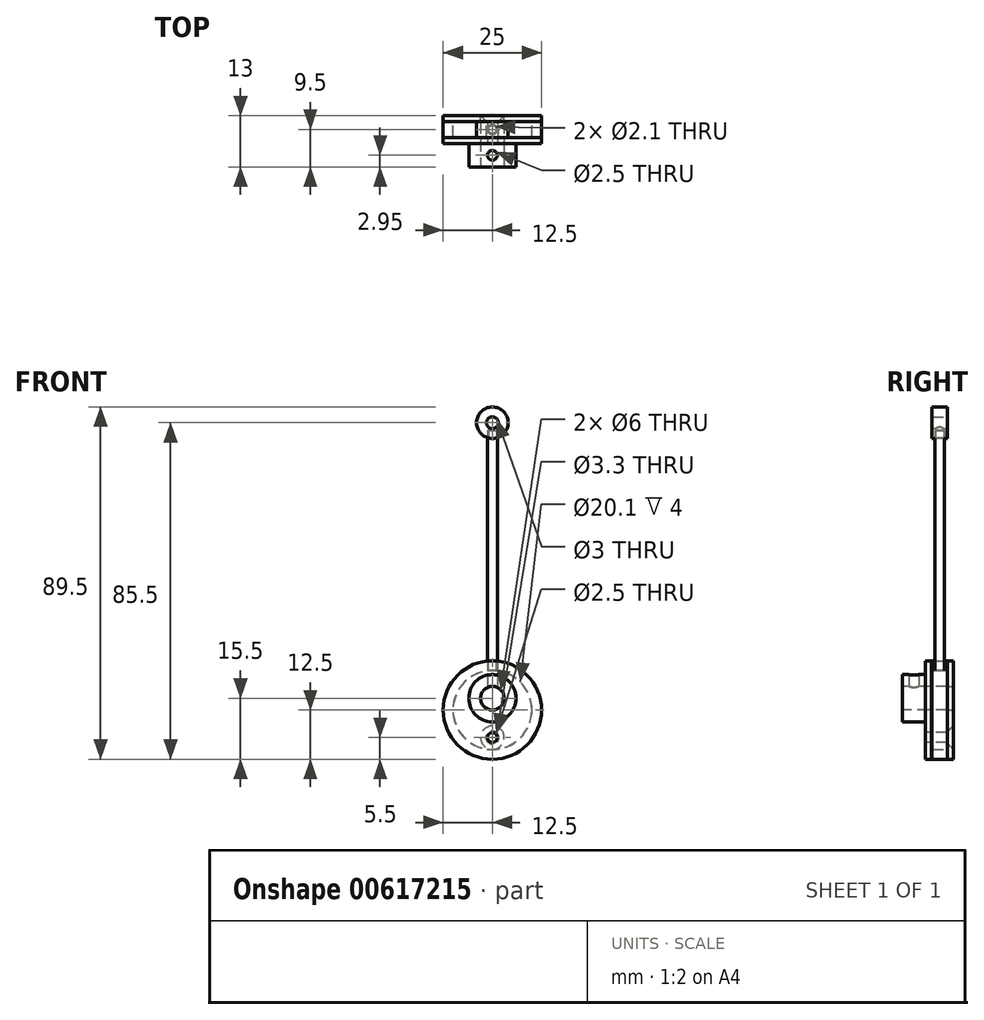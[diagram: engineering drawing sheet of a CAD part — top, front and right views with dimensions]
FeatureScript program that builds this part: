
annotation { "Feature Type Name" : "Feature", "Feature Type Description" : "" }
export const myFeature = defineFeature(function(context is Context, id is Id, definition is map)
    precondition{}
    {
        {
            var Q0;
            Q0=qCreatedBy(makeId("Front.planeOp"),FACE);
            var sketch = newSketch(context, id + "F0", { "sketchPlane" : qUnion([Q0])});
            skCircle(sketch, "E0", {"center": v(0, 0) * mm, "radius": 10 * mm});
            skSolve(sketch);
        }
        {
            var Q0;
            Q0 = qSketchRegion(id + "F0", true);
            extrude(context, id + "F1", {"entities" : qUnion([Q0]), "depth" : 4.1 * mm, "offsetDistance" : 25 * mm});
        }
        {
            var Q0;
            Q0=makeQuery(id+"F1.opExtrude","CAP_FACE",FACE,{"disambiguationData":[OSD([sQuery(id+"F0.wireOp",EDGE,"E0")])],"isStart":false});
            var sketch = newSketch(context, id + "F2", { "sketchPlane" : qUnion([Q0])});
            skCircle(sketch, "E1", {"center": v(0, 0) * mm, "radius": 12.5 * mm});
            skSolve(sketch);
        }
        {
            var Q0;
            Q0 = qSketchRegion(id + "F2", true);
            extrude(context, id + "F3", {"entities" : qUnion([Q0]), "operationType" : NewBodyOperationType.ADD, "depth" : 1.5 * mm, "offsetDistance" : 25 * mm});
        }
        {
            var Q0;
            Q0=makeQuery(id+"F3.opExtrude","CAP_FACE",FACE,{"disambiguationData":[OSD([sQuery(id+"F2.wireOp",EDGE,"E1")])],"isStart":false});
            var sketch = newSketch(context, id + "F4", { "sketchPlane" : qUnion([Q0])});
            skCircle(sketch, "E2", {"center": v(0, 3) * mm, "radius": 6 * mm});
            skSolve(sketch);
        }
        {
            var Q0;
            Q0 = qSketchRegion(id + "F4", true);
            extrude(context, id + "F5", {"entities" : qUnion([Q0]), "operationType" : NewBodyOperationType.ADD, "depth" : (11.5 - 1.5 - 4.1) * mm, "offsetDistance" : 25 * mm});
        }
        {
            var Q0;
            Q0=makeQuery(id+"F5.opExtrude","CAP_FACE",FACE,{"disambiguationData":[OSD([sQuery(id+"F4.wireOp",EDGE,"E2")])],"isStart":false});
            var sketch = newSketch(context, id + "F6", { "sketchPlane" : qUnion([Q0])});
            skPoint(sketch, "E3", {"position": v(0, 3) * mm});
            skSolve(sketch);
        }
        {
            var Q0;
            Q0=sQuery(id+"F6.wireOp",VERTEX,"E3");
            var Q1;
            Q1=makeQuery(id+"F1.opExtrude","SWEPT_BODY",BODY,{"disambiguationData":[OSD([sQuery(id+"F0.wireOp",EDGE,"E0")])]});
            hole(context, id + "F7", {"style" : HoleStyle.SIMPLE, "endStyle" : HoleEndStyle.THROUGH, "standardTappedOrClearance" : lookupTablePath({ "standard" : "ISO", "size" : "6", "type" : "Drilled" }), "standardBlindInLast" : lookupTablePath({ "standard" : "ISO", "size" : "6", "type" : "Drilled" }), "holeDiameter" : 6 * mm, "majorDiameter" : 3 * mm, "isTappedThrough" : true, "tappedDepth" : 6 * mm, "tapClearance" : 2, "locations" : qUnion([Q0]), "scope" : qUnion([Q1])});
        }
        {
            var Q0;
            Q0=makeQuery(id+"F3.opExtrude","CAP_FACE",FACE,{"disambiguationData":[OSD([sQuery(id+"F2.wireOp",EDGE,"E1")])],"isStart":false});
            var sketch = newSketch(context, id + "F8", { "sketchPlane" : qUnion([Q0])});
            skLineSegment(sketch, "E4", {"start": v(0, 0) * mm, "end": v(0, -7) * mm, "construction": true});
            skSolve(sketch);
        }
        {
            var Q0;
            Q0=sQuery(id+"F8.wireOp",VERTEX,"E4.end");
            var Q1;
            Q1=makeQuery(id+"F1.opExtrude","SWEPT_BODY",BODY,{"disambiguationData":[OSD([sQuery(id+"F0.wireOp",EDGE,"E0")])]});
            hole(context, id + "F9", {"style" : HoleStyle.SIMPLE, "endStyle" : HoleEndStyle.THROUGH, "standardTappedOrClearance" : lookupTablePath({ "standard" : "ISO", "engagement" : "75%", "pitch" : "0.5 mm", "size" : "M3", "type" : "Tapped" }), "standardBlindInLast" : lookupTablePath({ "standard" : "ISO", "engagement" : "75%", "pitch" : "0.5 mm", "size" : "M3", "type" : "Tapped" }), "holeDiameter" : 2.5 * mm, "majorDiameter" : 3 * mm, "showTappedDepth" : true, "isTappedThrough" : true, "tappedDepth" : 6 * mm, "tapClearance" : 2, "locations" : qUnion([Q0]), "scope" : qUnion([Q1])});
        }
        {
            var Q0;
            Q0=makeQuery(id+"F5.opExtrude","SWEPT_FACE",FACE,{"disambiguationData":[OSD([sQuery(id+"F4.wireOp",EDGE,"E2")])]});
            cPlane(context, id + "F10", {"entities" : qUnion([Q0]), "cplaneType" : CPlaneType.LINE_ANGLE, "offset" : 25 * mm, "angle" : 0 * degree, "width" : 150 * mm, "height" : 150 * mm});
        }
        {
            var Q0;
            Q0=qCreatedBy(id+"F10.planeOp",FACE);
            var sketch = newSketch(context, id + "F11", { "sketchPlane" : qUnion([Q0])});
            skLineSegment(sketch, "E5", {"start": v(0, -5.6) * mm, "end": v(0, -11.5) * mm, "construction": true});
            skPoint(sketch, "E6", {"position": v(0, -8.55) * mm});
            skSolve(sketch);
        }
        {
            var Q0;
            Q0=sQuery(id+"F11.wireOp",VERTEX,"E6");
            var Q1;
            Q1=makeQuery(id+"F1.opExtrude","SWEPT_BODY",BODY,{"disambiguationData":[OSD([sQuery(id+"F0.wireOp",EDGE,"E0")])]});
            hole(context, id + "F12", {"style" : HoleStyle.SIMPLE, "endStyle" : HoleEndStyle.THROUGH, "oppositeDirection" : true, "standardTappedOrClearance" : lookupTablePath({ "standard" : "ISO", "engagement" : "75%", "pitch" : "0.5 mm", "size" : "M3", "type" : "Tapped" }), "standardBlindInLast" : lookupTablePath({ "standard" : "ISO", "engagement" : "75%", "pitch" : "0.5 mm", "size" : "M3", "type" : "Tapped" }), "holeDiameter" : 2.5 * mm, "majorDiameter" : 3 * mm, "showTappedDepth" : true, "isTappedThrough" : true, "tappedDepth" : 6 * mm, "tapClearance" : 2, "locations" : qUnion([Q0]), "scope" : qUnion([Q1])});
        }
        {
            var Q0;
            Q0=makeQuery(id+"F1.opExtrude","CAP_FACE",FACE,{"disambiguationData":[OSD([sQuery(id+"F0.wireOp",EDGE,"E0")])],"isStart":true});
            var sketch = newSketch(context, id + "F13", { "sketchPlane" : qUnion([Q0])});
            skCircle(sketch, "E7", {"center": v(0, 0) * mm, "radius": 12.5 * mm});
            skSolve(sketch);
        }
        {
            var Q0;
            Q0 = qSketchRegion(id + "F13", true);
            extrude(context, id + "F14", {"entities" : qUnion([Q0]), "depth" : 1.5 * mm, "offsetDistance" : 25 * mm});
        }
        {
            var Q0;
            Q0=makeQuery(id+"F14.opExtrude","CAP_FACE",FACE,{"disambiguationData":[OSD([sQuery(id+"F13.wireOp",EDGE,"E7")])],"isStart":false});
            var sketch = newSketch(context, id + "F15", { "sketchPlane" : qUnion([Q0])});
            skPoint(sketch, "E8", {"position": v(0, 3) * mm});
            skPoint(sketch, "E9", {"position": v(0, -7) * mm});
            skSolve(sketch);
        }
        {
            var Q0;
            Q0=sQuery(id+"F15.wireOp",VERTEX,"E9");
            var Q1;
            Q1=makeQuery(id+"F14.opExtrude","SWEPT_BODY",BODY,{"disambiguationData":[OSD([sQuery(id+"F13.wireOp",EDGE,"E7")])]});
            hole(context, id + "F16", {"style" : HoleStyle.C_SINK, "endStyle" : HoleEndStyle.THROUGH, "holeDiameter" : 3.3 * mm, "cSinkDiameter" : 6 * mm, "cSinkAngle" : 90 * degree, "majorDiameter" : 3 * mm, "isTappedThrough" : true, "tappedDepth" : 6 * mm, "tapClearance" : 2, "locations" : qUnion([Q0]), "scope" : qUnion([Q1])});
        }
        {
            var Q0;
            Q0=sQuery(id+"F15.wireOp",VERTEX,"E8");
            var Q1;
            Q1=makeQuery(id+"F14.opExtrude","SWEPT_BODY",BODY,{"disambiguationData":[OSD([sQuery(id+"F13.wireOp",EDGE,"E7")])]});
            hole(context, id + "F17", {"style" : HoleStyle.SIMPLE, "endStyle" : HoleEndStyle.THROUGH, "standardTappedOrClearance" : lookupTablePath({ "standard" : "ISO", "size" : "6", "type" : "Drilled" }), "standardBlindInLast" : lookupTablePath({ "standard" : "ISO", "size" : "6", "type" : "Drilled" }), "holeDiameter" : 6 * mm, "majorDiameter" : 5 * mm, "isTappedThrough" : true, "tappedDepth" : 6 * mm, "tapClearance" : 2, "locations" : qUnion([Q0]), "scope" : qUnion([Q1])});
        }
        {
            var Q0;
            Q0=qCreatedBy(makeId("Front.planeOp"),FACE);
            cPlane(context, id + "F18", {"entities" : qUnion([Q0]), "cplaneType" : CPlaneType.OFFSET, "offset" : 2 * mm, "width" : 150 * mm, "height" : 150 * mm});
        }
        {
            var Q0;
            Q0=qCreatedBy(id+"F18.planeOp",FACE);
            var sketch = newSketch(context, id + "F19", { "sketchPlane" : qUnion([Q0])});
            skCircle(sketch, "E10", {"center": v(0, 0) * mm, "radius": 10.05 * mm});
            skCircle(sketch, "E11", {"center": v(0, 0) * mm, "radius": 12.5 * mm});
            skSolve(sketch);
        }
        {
            var Q0;
            Q0 = qSketchRegion(id + "F19", true);
            extrude(context, id + "F20", {"entities" : qUnion([Q0]), "endBound" : BoundingType.SYMMETRIC, "depth" : 4 * mm, "offsetDistance" : 25 * mm});
        }
        {
            var Q0;
            Q0=qCreatedBy(makeId("Top.planeOp"),FACE);
            cPlane(context, id + "F21", {"entities" : qUnion([Q0]), "cplaneType" : CPlaneType.OFFSET, "offset" : 12.5 * mm, "width" : 150 * mm, "height" : 150 * mm});
        }
        {
            var Q0;
            Q0=qCreatedBy(id+"F21.planeOp",FACE);
            var sketch = newSketch(context, id + "F22", { "sketchPlane" : qUnion([Q0])});
            skLineSegment(sketch, "E12", {"start": v(0, -4) * mm, "end": v(0, 0) * mm, "construction": true});
            skPoint(sketch, "E13", {"position": v(0, -2) * mm});
            skSolve(sketch);
        }
        {
            var Q0;
            Q0=sQuery(id+"F22.wireOp",VERTEX,"E13");
            var Q1;
            Q1=makeQuery(id+"F20.opExtrude","SWEPT_BODY",BODY,{"disambiguationData":[OSD([sQuery(id+"F19.wireOp",EDGE,"E10"),sQuery(id+"F19.wireOp",EDGE,"E11")])]});
            hole(context, id + "F23", {"style" : HoleStyle.SIMPLE, "endStyle" : HoleEndStyle.BLIND, "standardTappedOrClearance" : lookupTablePath({ "standard" : "ISO", "size" : "2.1", "type" : "Drilled" }), "standardBlindInLast" : lookupTablePath({ "standard" : "ISO", "size" : "2.1", "type" : "Drilled" }), "holeDiameter" : 2.1 * mm, "majorDiameter" : 5 * mm, "holeDepth" : 3 * mm, "isTappedThrough" : true, "tappedDepth" : 6 * mm, "tapClearance" : 2, "locations" : qUnion([Q0]), "scope" : qUnion([Q1])});
        }
        {
            var Q0;
            Q0=qCreatedBy(id+"F18.planeOp",FACE);
            var sketch = newSketch(context, id + "F24", { "sketchPlane" : qUnion([Q0])});
            skLineSegment(sketch, "E14", {"start": v(0, 0) * mm, "end": v(0, 73) * mm, "construction": true});
            skCircle(sketch, "E15", {"center": v(0, 73) * mm, "radius": 1.5 * mm});
            skCircle(sketch, "E16", {"center": v(0, 73) * mm, "radius": 4 * mm});
            skPoint(sketch, "E17", {"position": v(0, 69) * mm});
            skSolve(sketch);
        }
        {
            var Q0;
            Q0 = qSketchRegion(id + "F24", true);
            extrude(context, id + "F25", {"entities" : qUnion([Q0]), "endBound" : BoundingType.SYMMETRIC, "depth" : 4 * mm, "offsetDistance" : 25 * mm});
        }
        {
            var Q0;
            Q0=qCreatedBy(makeId("Top.planeOp"),FACE);
            var Q1;
            Q1=sQuery(id+"F24.wireOp",VERTEX,"E17");
            cPlane(context, id + "F26", {"entities" : qUnion([Q0, Q1]), "cplaneType" : CPlaneType.PLANE_POINT, "offset" : 25 * mm, "width" : 150 * mm, "height" : 150 * mm});
        }
        {
            var Q0;
            Q0=qCreatedBy(id+"F26.planeOp",FACE);
            var sketch = newSketch(context, id + "F27", { "sketchPlane" : qUnion([Q0])});
            skPoint(sketch, "E18", {"position": v(0, -2) * mm});
            skSolve(sketch);
        }
        {
            var Q0;
            Q0=sQuery(id+"F27.wireOp",VERTEX,"E18");
            var Q1;
            Q1=makeQuery(id+"F25.opExtrude","SWEPT_BODY",BODY,{"disambiguationData":[OSD([sQuery(id+"F24.wireOp",EDGE,"E15"),sQuery(id+"F24.wireOp",EDGE,"E16")])]});
            hole(context, id + "F28", {"style" : HoleStyle.SIMPLE, "endStyle" : HoleEndStyle.BLIND, "oppositeDirection" : true, "standardTappedOrClearance" : lookupTablePath({ "standard" : "ISO", "size" : "2.1", "type" : "Drilled" }), "standardBlindInLast" : lookupTablePath({ "standard" : "ISO", "size" : "2.1", "type" : "Drilled" }), "holeDiameter" : 2.1 * mm, "majorDiameter" : 5 * mm, "holeDepth" : 3 * mm, "isTappedThrough" : true, "tappedDepth" : 6 * mm, "tapClearance" : 2, "locations" : qUnion([Q0]), "scope" : qUnion([Q1])});
        }
        {
            var Q0;
            Q0=qCreatedBy(id+"F18.planeOp",FACE);
            var sketch = newSketch(context, id + "F29", { "sketchPlane" : qUnion([Q0])});
            skLineSegment(sketch, "E19.0", {"start": v(0, 0) * mm, "end": v(0, 73) * mm, "construction": true});
            skLineSegment(sketch, "E20.bottom", {"start": v(1.25, 71.05) * mm, "end": v(0, 71.05) * mm});
            skLineSegment(sketch, "E20.top", {"start": v(1.25, 10.05) * mm, "end": v(0, 10.05) * mm});
            skLineSegment(sketch, "E20.left", {"start": v(1.25, 71.05) * mm, "end": v(1.25, 10.05) * mm});
            skLineSegment(sketch, "E20.right", {"start": v(0, 71.05) * mm, "end": v(0, 10.05) * mm});
            skPoint(sketch, "E21", {"position": v(0, 71.5) * mm});
            skSolve(sketch);
        }
        {
            var Q0;
            Q0 = qSketchRegion(id + "F29", true);
            var Q1;
            Q1=sQuery(id+"F29.wireOp",EDGE,"E19.0");
            revolve(context, id + "F30", {"entities" : qUnion([Q0]), "axis" : qUnion([Q1]), "revolveType" : RevolveType.FULL});
        }
    });
